FCSTD DOCUMENT  (FreeCAD 1.0R39319 (Git))
Label: 02_Fuselage
License: All rights reserved
LicenseURL: https://en.wikipedia.org/wiki/All_rights_reserved
objects: Sketcher::SketchObject×1, PartDesign::Body×1
note: 3 computed .brp shape members not serialized (recipe doc carries the construction recipe); baked Part::Feature solids carry a one-line shape summary decoded from their .brp

FEATURE [Sketcher::SketchObject] Sketch
  ArcFitTolerance = 1e-06
  AttachmentSupport = -> [XZ_Plane]
  FullyConstrained = true
  MakeInternals = false
  MapMode = 5
  Placement = pos=(0,0,0) rot=(1,0,0;1.5708rad)
  sketch-geometry (12):
    g0: LineSegment [constr] StartX=0 StartY=0 StartZ=0 EndX=2000 EndY=0 EndZ=0
    g1: LineSegment [constr] StartX=0 StartY=0 StartZ=0 EndX=-2000 EndY=0 EndZ=0
    g2: LineSegment StartX=-1250 StartY=300 StartZ=0 EndX=450 EndY=300 EndZ=0
    g3: GeomPoint [constr] X=1250 Y=0 Z=0
    g4: GeomPoint [constr] X=-1250 Y=0 Z=0
    g5: GeomPoint [constr] X=450 Y=300 Z=0
    g6: GeomPoint [constr] X=450 Y=0 Z=0
    g7: ArcOfEllipse CenterX=450 CenterY=0 CenterZ=0 NormalX=0 NormalY=0 NormalZ=1 MajorRadius=800 MinorRadius=300 AngleXU=3.14159 StartAngle=3.14159 EndAngle=4.71239
    g8: LineSegment [constr] StartX=-350 StartY=0 StartZ=0 EndX=1250 EndY=0 EndZ=0
    g9: LineSegment [constr] StartX=450 StartY=-300 StartZ=0 EndX=450 EndY=300 EndZ=0
    g10: GeomPoint [constr] X=-291.62 Y=0 Z=0
    g11: GeomPoint [constr] X=1191.62 Y=0 Z=0
  constraints (22):
    c: Distance(g0) = 2000
    c: Coincident(g0,g-1)
    c: Horizontal(g0)
    c: Distance(g1) = 2000
    c: Coincident(g1,g0)
    c: PointOnObject(g1,g-1)
    c: Horizontal(g2)
    c: Distance(g1,g2) = 300
    c: DistanceX(g2,g-1) = 1250
    c: PointOnObject(g3,g0)
    c: Distance(g3,g-2) = 1250
    c: PointOnObject(g4,g1)
    c: DistanceX(g4,g0) = 1250
    c: PointOnObject(g5,g2)
    c: PointOnObject(g6,g0)
    c: InternalAlignment(g8-g11 -> g7) x4
    c: Coincident(g7,g6)
    c: Coincident(g8,g3)
    c: Coincident(g9,g5)
    c: PointOnObject(g7,g0)
    c: Coincident(g2,g7)
    c: DistanceX(g6,g7) = 800
FEATURE [PartDesign::Body] Body
  AllowCompound = false
  Group = -> [Sketch]
  Origin = -> Origin
